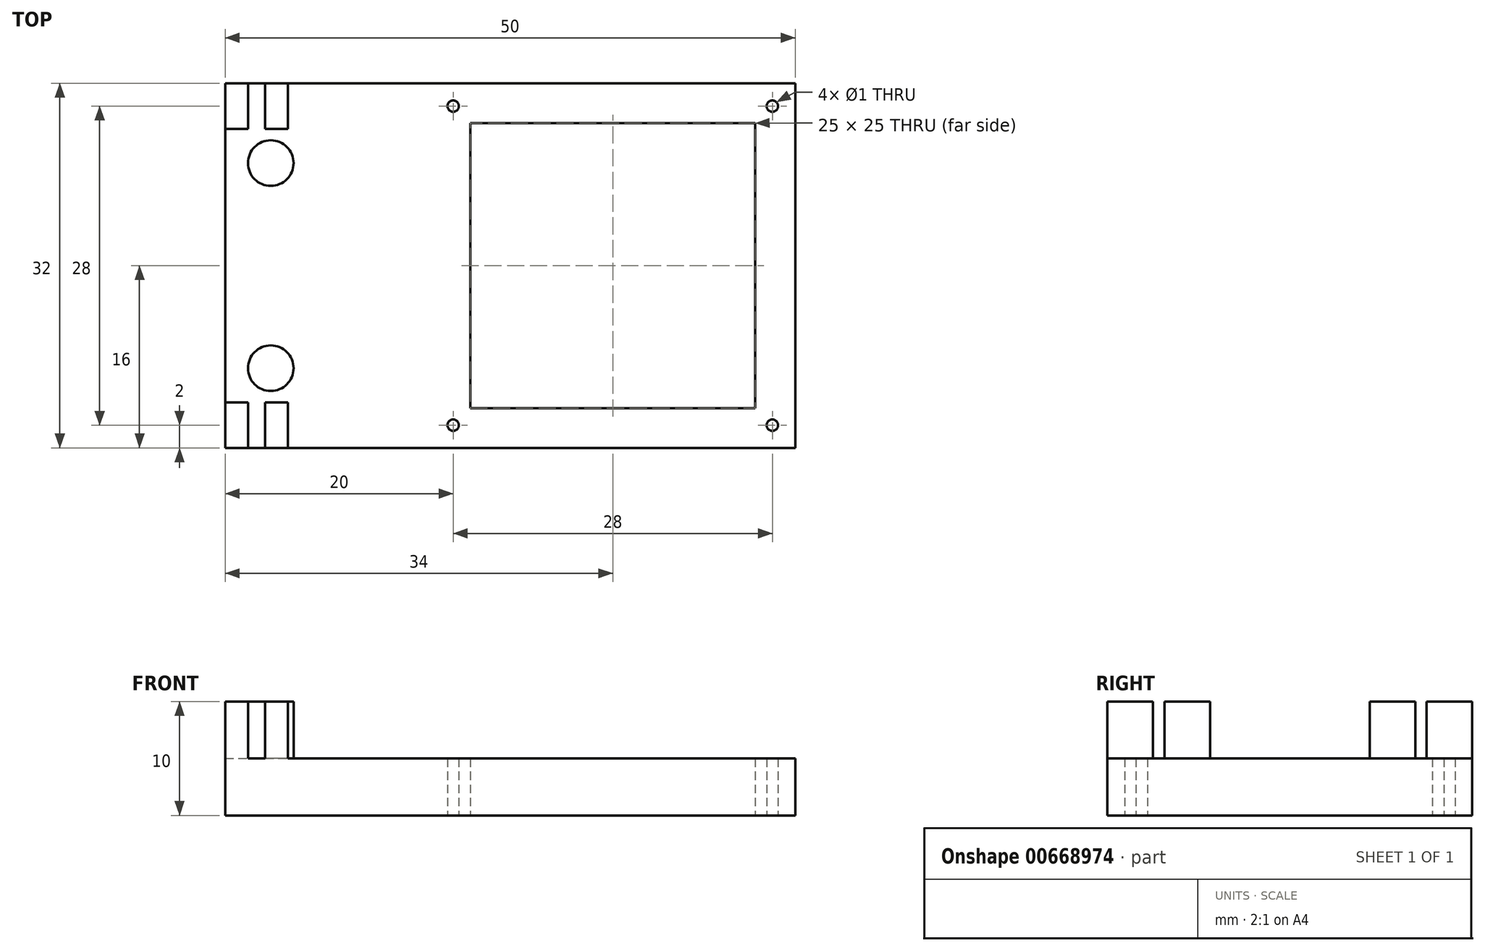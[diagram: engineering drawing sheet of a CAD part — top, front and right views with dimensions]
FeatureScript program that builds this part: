
annotation { "Feature Type Name" : "Feature", "Feature Type Description" : "" }
export const myFeature = defineFeature(function(context is Context, id is Id, definition is map)
    precondition{}
    {
        {
            var Q0;
            Q0=qCreatedBy(makeId("Top.planeOp"),FACE);
            var sketch = newSketch(context, id + "F0", { "sketchPlane" : qUnion([Q0])});
            skLineSegment(sketch, "E0.bottom", {"start": v(0, 0) * mm, "end": v(50, 0) * mm});
            skLineSegment(sketch, "E0.top", {"start": v(0, 32) * mm, "end": v(50, 32) * mm});
            skLineSegment(sketch, "E0.left", {"start": v(0, 0) * mm, "end": v(0, 32) * mm});
            skLineSegment(sketch, "E0.right", {"start": v(50, 0) * mm, "end": v(50, 32) * mm});
            skLineSegment(sketch, "E1", {"start": v(0, 16) * mm, "end": v(50, 16) * mm, "construction": true});
            skCircle(sketch, "E2", {"center": v(48, 30) * mm, "radius": 0.5 * mm});
            skLineSegment(sketch, "E3", {"start": v(34, 32) * mm, "end": v(34, 16) * mm, "construction": true});
            skCircle(sketch, "E4.MirrorC", {"center": v(20, 30) * mm, "radius": 0.5 * mm});
            skCircle(sketch, "E5.MirrorC", {"center": v(48, 2) * mm, "radius": 0.5 * mm});
            skCircle(sketch, "E6.MirrorC", {"center": v(20, 2) * mm, "radius": 0.5 * mm});
            skLineSegment(sketch, "E7.bottom", {"start": v(46.5, 28.5) * mm, "end": v(21.5, 28.5) * mm});
            skLineSegment(sketch, "E7.top", {"start": v(46.5, 3.5) * mm, "end": v(21.5, 3.5) * mm});
            skLineSegment(sketch, "E7.left", {"start": v(46.5, 28.5) * mm, "end": v(46.5, 3.5) * mm});
            skLineSegment(sketch, "E7.right", {"start": v(21.5, 28.5) * mm, "end": v(21.5, 3.5) * mm});
            skPoint(sketch, "E7.middle", {"position": v(34, 16) * mm});
            skSolve(sketch);
        }
        {
            var Q0;
            Q0=makeQuery(id+"F0.imprint","IMPRINT",FACE,{"disambiguationData":[TD([[makeQuery(id+"F0.imprint","IMPRINT",EDGE,{"derivedFrom":sQuery(id+"F0.wireOp",EDGE,"E0.bottom")}),1.0]])]});
            extrude(context, id + "F1", {"entities" : qUnion([Q0]), "depth" : 5 * mm, "offsetDistance" : 25 * mm});
        }
        {
            var Q0;
            Q0=makeQuery(id+"F1.opExtrude","CAP_FACE",FACE,{"disambiguationData":[OSD([sQuery(id+"F0.wireOp",EDGE,"E0.bottom"),sQuery(id+"F0.wireOp",EDGE,"E0.top"),sQuery(id+"F0.wireOp",EDGE,"E0.left"),sQuery(id+"F0.wireOp",EDGE,"E0.right"),sQuery(id+"F0.wireOp",EDGE,"E2"),sQuery(id+"F0.wireOp",EDGE,"E4.MirrorC"),sQuery(id+"F0.wireOp",EDGE,"E5.MirrorC"),sQuery(id+"F0.wireOp",EDGE,"E6.MirrorC"),sQuery(id+"F0.wireOp",EDGE,"E7.bottom"),sQuery(id+"F0.wireOp",EDGE,"E7.top"),sQuery(id+"F0.wireOp",EDGE,"E7.left"),sQuery(id+"F0.wireOp",EDGE,"E7.right")])],"isStart":false});
            var sketch = newSketch(context, id + "F2", { "sketchPlane" : qUnion([Q0])});
            skLineSegment(sketch, "E8", {"start": v(0, 16) * mm, "end": v(50, 16) * mm, "construction": true});
            skLineSegment(sketch, "E9.bottom", {"start": v(0, 32) * mm, "end": v(2, 32) * mm});
            skLineSegment(sketch, "E9.top", {"start": v(0, 28) * mm, "end": v(2, 28) * mm});
            skLineSegment(sketch, "E9.left", {"start": v(0, 32) * mm, "end": v(0, 28) * mm});
            skLineSegment(sketch, "E9.right", {"start": v(2, 32) * mm, "end": v(2, 28) * mm});
            skLineSegment(sketch, "E10.bottom", {"start": v(5.5, 28) * mm, "end": v(3.5, 28) * mm});
            skLineSegment(sketch, "E10.top", {"start": v(5.5, 32) * mm, "end": v(3.5, 32) * mm});
            skLineSegment(sketch, "E10.left", {"start": v(5.5, 28) * mm, "end": v(5.5, 32) * mm});
            skLineSegment(sketch, "E10.right", {"start": v(3.5, 28) * mm, "end": v(3.5, 32) * mm});
            skCircle(sketch, "E11", {"center": v(4, 25) * mm, "radius": 2 * mm});
            skLineSegment(sketch, "E12.MirrorCS", {"start": v(0, 4) * mm, "end": v(2, 4) * mm});
            skLineSegment(sketch, "E13.MirrorCS", {"start": v(2, 0) * mm, "end": v(2, 4) * mm});
            skLineSegment(sketch, "E14.MirrorCS", {"start": v(0, 0) * mm, "end": v(2, 0) * mm});
            skLineSegment(sketch, "E15.MirrorCS", {"start": v(5.5, 4) * mm, "end": v(5.5, 0) * mm});
            skLineSegment(sketch, "E16.MirrorCS", {"start": v(5.5, 0) * mm, "end": v(3.5, 0) * mm});
            skLineSegment(sketch, "E17.MirrorCS", {"start": v(5.5, 4) * mm, "end": v(3.5, 4) * mm});
            skCircle(sketch, "E18.MirrorC", {"center": v(4, 7) * mm, "radius": 2 * mm});
            skLineSegment(sketch, "E19.MirrorCS", {"start": v(0, 0) * mm, "end": v(0, 4) * mm});
            skLineSegment(sketch, "E20.MirrorCS", {"start": v(3.5, 4) * mm, "end": v(3.5, 0) * mm});
            skSolve(sketch);
        }
        {
            var Q0;
            Q0 = qSketchRegion(id + "F2", true);
            extrude(context, id + "F3", {"entities" : qUnion([Q0]), "operationType" : NewBodyOperationType.ADD, "depth" : 5 * mm, "offsetDistance" : 25 * mm});
        }
    });
